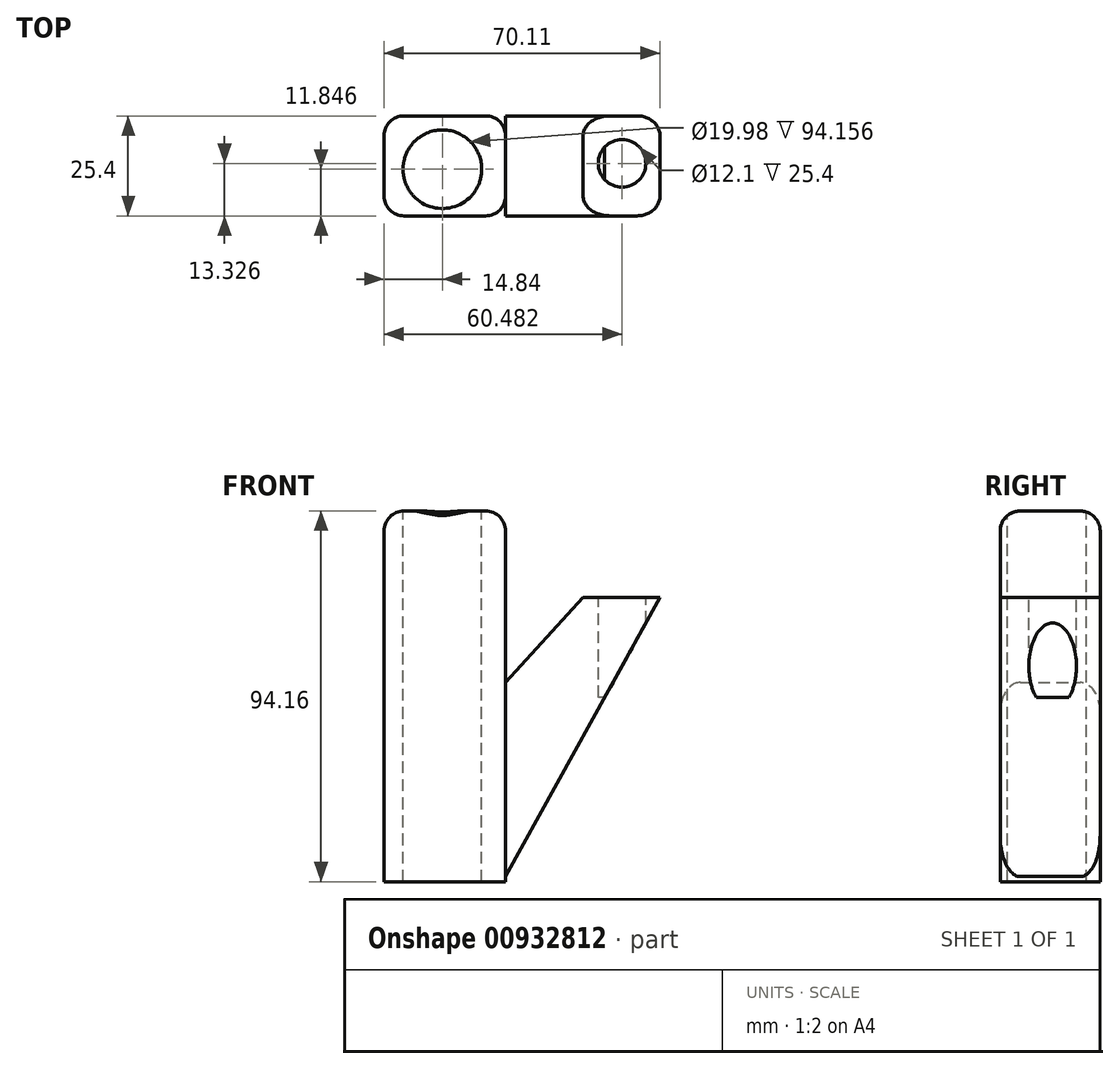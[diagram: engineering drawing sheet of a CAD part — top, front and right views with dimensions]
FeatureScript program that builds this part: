
annotation { "Feature Type Name" : "Feature", "Feature Type Description" : "" }
export const myFeature = defineFeature(function(context is Context, id is Id, definition is map)
    precondition{}
    {
        {
            var Q0;
            Q0=qCreatedBy(makeId("Front.planeOp"),FACE);
            var sketch = newSketch(context, id + "F0", { "sketchPlane" : qUnion([Q0])});
            skLineSegment(sketch, "E0", {"start": v(0, 0) * mm, "end": v(0, 173.04) * mm, "construction": true});
            skLineSegment(sketch, "E1", {"start": v(0, 112) * mm, "end": v(-30.9, 112) * mm});
            skLineSegment(sketch, "E2", {"start": v(-30.9, 112) * mm, "end": v(-30.9, 17.84) * mm});
            skLineSegment(sketch, "E3", {"start": v(-30.9, 17.84) * mm, "end": v(0, 17.84) * mm});
            skLineSegment(sketch, "E4", {"start": v(0, 112) * mm, "end": v(0, 17.84) * mm});
            skSolve(sketch);
        }
        {
            var Q0;
            Q0 = qSketchRegion(id + "F0", true);
            var sketch = newSketch(context, id + "F1", { "sketchPlane" : qUnion([Q0])});
            skLineSegment(sketch, "E5", {"start": v(0, 68.45) * mm, "end": v(19.66, 90.03) * mm});
            skLineSegment(sketch, "E6", {"start": v(19.66, 90.03) * mm, "end": v(39.2, 90.03) * mm});
            skLineSegment(sketch, "E7", {"start": v(39.2, 90.03) * mm, "end": v(0, 19.13) * mm});
            skLineSegment(sketch, "E8", {"start": v(0, 19.13) * mm, "end": v(0, 19.13) * mm});
            skLineSegment(sketch, "E9", {"start": v(0, 68.45) * mm, "end": v(0, 19.13) * mm});
            skSolve(sketch);
        }
        {
            var Q0;
            Q0 = qSketchRegion(id + "F1", true);
            var Q1;
            Q1=makeQuery(id+"F0.imprint","IMPRINT",FACE,{"disambiguationData":[TD([[makeQuery(id+"F0.imprint","IMPRINT",EDGE,{"derivedFrom":sQuery(id+"F0.wireOp",EDGE,"E1")}),1.0]])]});
            extrude(context, id + "F2", {"entities" : qUnion([Q0, Q1]), "depth" : 25.4 * mm, "offsetDistance" : 25.4 * mm});
        }
        {
            var Q0;
            Q0=makeQuery(id+"F2.opExtrude","CAP_EDGE",EDGE,{"disambiguationData":[OSD([sQuery(id+"F0.wireOp",EDGE,"E4")])],"isStart":false});
            var Q1;
            Q1=makeQuery(id+"F2.opExtrude","CAP_EDGE",EDGE,{"disambiguationData":[OSD([sQuery(id+"F0.wireOp",EDGE,"E2")])],"isStart":false});
            var Q2;
            Q2=makeQuery(id+"F2.opExtrude","CAP_EDGE",EDGE,{"disambiguationData":[OSD([sQuery(id+"F1.wireOp",EDGE,"E7")])],"isStart":true});
            var Q3;
            Q3=makeQuery(id+"F2.opExtrude","CAP_EDGE",EDGE,{"disambiguationData":[OSD([sQuery(id+"F1.wireOp",EDGE,"E7")])],"isStart":false});
            var Q4;
            Q4=makeQuery(id+"F2.opExtrude","CAP_EDGE",EDGE,{"disambiguationData":[OSD([sQuery(id+"F1.wireOp",EDGE,"E5")])],"isStart":false});
            var Q5;
            Q5=makeQuery(id+"F2.opExtrude","CAP_EDGE",EDGE,{"disambiguationData":[OSD([sQuery(id+"F1.wireOp",EDGE,"E5")])],"isStart":true});
            var Q6;
            Q6=makeQuery(id+"F2.opExtrude","CAP_EDGE",EDGE,{"disambiguationData":[OSD([sQuery(id+"F0.wireOp",EDGE,"E4")])],"isStart":true});
            var Q7;
            Q7=makeQuery(id+"F2.opExtrude","SWEPT_EDGE",EDGE,{"disambiguationData":[OSD([sQuery(id+"F0.wireOp",EDGE,"E1"),sQuery(id+"F0.wireOp",EDGE,"E2")])]});
            var Q8;
            Q8=makeQuery(id+"F2.opExtrude","CAP_EDGE",EDGE,{"disambiguationData":[OSD([sQuery(id+"F0.wireOp",EDGE,"E1")])],"isStart":false});
            var Q9;
            Q9=makeQuery(id+"F2.opExtrude","SWEPT_EDGE",EDGE,{"disambiguationData":[OSD([sQuery(id+"F0.wireOp",EDGE,"E1"),sQuery(id+"F0.wireOp",EDGE,"E4")])]});
            var Q10;
            Q10=makeQuery(id+"F2.opExtrude","CAP_EDGE",EDGE,{"disambiguationData":[OSD([sQuery(id+"F0.wireOp",EDGE,"E1")])],"isStart":true});
            var Q11;
            Q11=makeQuery(id+"F2.opExtrude","CAP_EDGE",EDGE,{"disambiguationData":[OSD([sQuery(id+"F0.wireOp",EDGE,"E2")])],"isStart":true});
            fillet(context, id + "F3", {"entities" : qUnion([Q0, Q1, Q2, Q3, Q4, Q5, Q6, Q7, Q8, Q9, Q10, Q11]), "radius" : 5.08 * mm, "tangentPropagation" : true, "allowEdgeOverflow" : false});
        }
        {
            var Q0;
            Q0=makeQuery(id+"F2.opExtrude","SWEPT_FACE",FACE,{"disambiguationData":[OSD([sQuery(id+"F1.wireOp",EDGE,"E6")])]});
            var sketch = newSketch(context, id + "F4", { "sketchPlane" : qUnion([Q0])});
            skCircle(sketch, "E10", {"center": v(29.57, -12.07) * mm, "radius": 6.05 * mm});
            skSolve(sketch);
        }
        {
            var Q0;
            Q0 = qSketchRegion(id + "F4", true);
            extrude(context, id + "F5", {"entities" : qUnion([Q0]), "operationType" : NewBodyOperationType.REMOVE, "oppositeDirection" : true, "depth" : 25.4 * mm, "offsetDistance" : 25.4 * mm});
        }
        {
            var Q0;
            Q0=makeQuery(id+"F2.opExtrude","SWEPT_FACE",FACE,{"disambiguationData":[OSD([sQuery(id+"F0.wireOp",EDGE,"E1")])]});
            var sketch = newSketch(context, id + "F6", { "sketchPlane" : qUnion([Q0])});
            skCircle(sketch, "E11", {"center": v(-16.07, -13.55) * mm, "radius": 10 * mm});
            skSolve(sketch);
        }
        {
            var Q0;
            Q0 = qSketchRegion(id + "F6", true);
            extrude(context, id + "F7", {"entities" : qUnion([Q0]), "operationType" : NewBodyOperationType.REMOVE, "endBound" : BoundingType.THROUGH_ALL, "oppositeDirection" : true, "depth" : 25.4 * mm, "offsetDistance" : 25.4 * mm});
        }
    });
